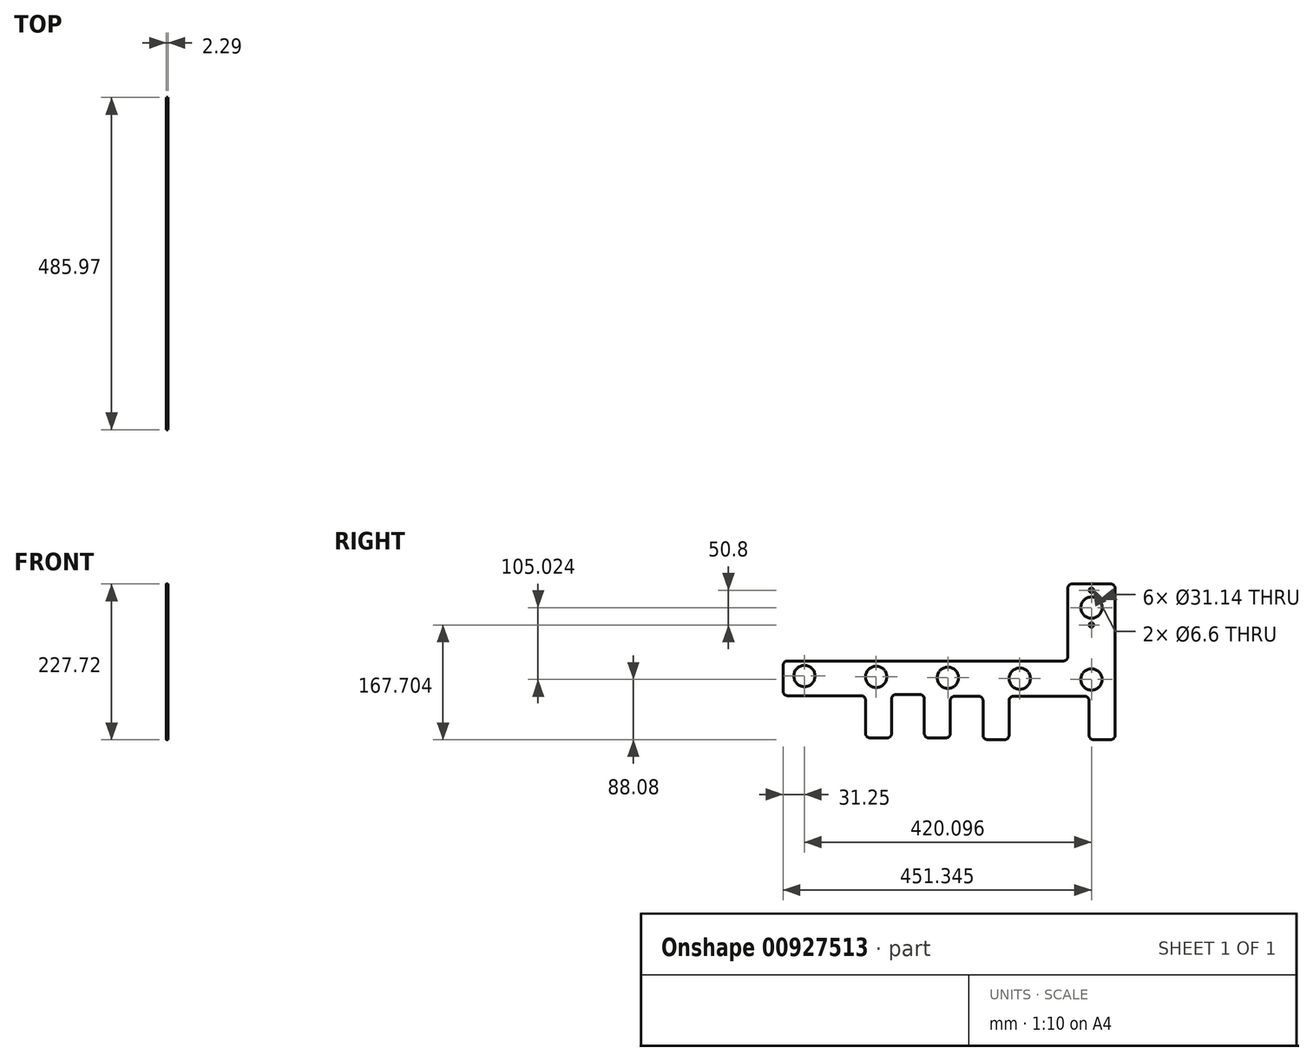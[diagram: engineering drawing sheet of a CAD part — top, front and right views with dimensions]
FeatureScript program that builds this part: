
annotation { "Feature Type Name" : "Feature", "Feature Type Description" : "" }
export const myFeature = defineFeature(function(context is Context, id is Id, definition is map)
    precondition{}
    {
        {
            var Q0;
            Q0=qCreatedBy(makeId("Right.planeOp"),FACE);
            var sketch = newSketch(context, id + "F0", { "sketchPlane" : qUnion([Q0])});
            skLineSegment(sketch, "E0.bottom", {"start": v(-215.45, 21.92) * mm, "end": v(188.58, 21.92) * mm});
            skLineSegment(sketch, "E0.top", {"start": v(-215.45, -28.88) * mm, "end": v(-107.45, -28.88) * mm});
            skLineSegment(sketch, "E0.left", {"start": v(-221.8, 15.57) * mm, "end": v(-221.8, -22.53) * mm});
            skCircle(sketch, "E1", {"center": v(-190.55, 0) * mm, "radius": 15.57 * mm});
            skCircle(sketch, "E2", {"center": v(-85.53, -1.27) * mm, "radius": 15.57 * mm});
            skCircle(sketch, "E3", {"center": v(19.5, -2.54) * mm, "radius": 15.57 * mm});
            skCircle(sketch, "E4", {"center": v(124.52, -3.81) * mm, "radius": 15.57 * mm});
            skCircle(sketch, "E5", {"center": v(229.55, -5.08) * mm, "radius": 15.57 * mm});
            skPoint(sketch, "E6.visualSharp", {"position": v(-221.8, 21.92) * mm});
            skArc(sketch, "E6.filletArc", {"start": v(-215.45, 21.92) * mm, "mid": v(-219.94, 20.06) * mm, "end": v(-221.8, 15.57) * mm});
            skPoint(sketch, "E7.visualSharp", {"position": v(264.17, 21.92) * mm});
            skLineSegment(sketch, "E8.left", {"start": v(-101.1, -35.23) * mm, "end": v(-101.1, -84.27) * mm});
            skLineSegment(sketch, "E8.right", {"start": v(108.95, -36) * mm, "end": v(108.95, -86.8) * mm});
            skArc(sketch, "E9.filletArc", {"start": v(-101.1, -35.23) * mm, "mid": v(-102.96, -30.74) * mm, "end": v(-107.45, -28.88) * mm});
            skLineSegment(sketch, "E10", {"start": v(115.3, -29.66) * mm, "end": v(219.72, -29.66) * mm});
            skPoint(sketch, "E11.visualSharp", {"position": v(108.95, -29.66) * mm});
            skArc(sketch, "E11.filletArc", {"start": v(115.3, -29.66) * mm, "mid": v(110.81, -31.52) * mm, "end": v(108.95, -36) * mm});
            skPoint(sketch, "E12.visualSharp", {"position": v(264.17, -29.66) * mm});
            skPoint(sketch, "E13.visualSharp", {"position": v(-221.8, -28.88) * mm});
            skArc(sketch, "E13.filletArc", {"start": v(-221.8, -22.53) * mm, "mid": v(-219.94, -27.02) * mm, "end": v(-215.45, -28.88) * mm});
            skPoint(sketch, "E14.visualSharp", {"position": v(-101.1, -90.62) * mm});
            skArc(sketch, "E14.filletArc", {"start": v(-101.1, -84.27) * mm, "mid": v(-99.24, -88.76) * mm, "end": v(-94.75, -90.62) * mm});
            skPoint(sketch, "E15.visualSharp", {"position": v(108.95, -93.16) * mm});
            skArc(sketch, "E15.filletArc", {"start": v(102.6, -93.16) * mm, "mid": v(107.1, -91.3) * mm, "end": v(108.95, -86.8) * mm});
            skLineSegment(sketch, "E16", {"start": v(70.85, -86.8) * mm, "end": v(70.85, -36) * mm});
            skLineSegment(sketch, "E17", {"start": v(-63, -84.27) * mm, "end": v(-63, -33.47) * mm});
            skLineSegment(sketch, "E18", {"start": v(22.97, -84.27) * mm, "end": v(22.97, -36) * mm});
            skLineSegment(sketch, "E19", {"start": v(-15.12, -84.27) * mm, "end": v(-15.12, -33.47) * mm});
            skLineSegment(sketch, "E20", {"start": v(102.6, -93.16) * mm, "end": v(77.2, -93.16) * mm});
            skLineSegment(sketch, "E21", {"start": v(16.62, -90.62) * mm, "end": v(-8.77, -90.62) * mm});
            skLineSegment(sketch, "E22", {"start": v(-69.35, -90.62) * mm, "end": v(-94.75, -90.62) * mm});
            skLineSegment(sketch, "E23", {"start": v(64.5, -29.66) * mm, "end": v(29.32, -29.66) * mm});
            skLineSegment(sketch, "E24", {"start": v(-21.47, -27.12) * mm, "end": v(-56.65, -27.12) * mm});
            skPoint(sketch, "E25.visualSharp", {"position": v(70.85, -93.16) * mm});
            skArc(sketch, "E25.filletArc", {"start": v(70.85, -86.8) * mm, "mid": v(72.71, -91.3) * mm, "end": v(77.2, -93.16) * mm});
            skPoint(sketch, "E26.visualSharp", {"position": v(70.85, -29.66) * mm});
            skArc(sketch, "E26.filletArc", {"start": v(70.85, -36) * mm, "mid": v(69, -31.52) * mm, "end": v(64.5, -29.66) * mm});
            skPoint(sketch, "E27.visualSharp", {"position": v(22.97, -29.66) * mm});
            skArc(sketch, "E27.filletArc", {"start": v(29.32, -29.66) * mm, "mid": v(24.83, -31.52) * mm, "end": v(22.97, -36) * mm});
            skPoint(sketch, "E28.visualSharp", {"position": v(22.97, -90.62) * mm});
            skArc(sketch, "E28.filletArc", {"start": v(16.62, -90.62) * mm, "mid": v(21.11, -88.76) * mm, "end": v(22.97, -84.27) * mm});
            skPoint(sketch, "E29.visualSharp", {"position": v(-15.12, -90.62) * mm});
            skArc(sketch, "E29.filletArc", {"start": v(-15.12, -84.27) * mm, "mid": v(-13.26, -88.76) * mm, "end": v(-8.77, -90.62) * mm});
            skPoint(sketch, "E30.visualSharp", {"position": v(-15.12, -27.12) * mm});
            skArc(sketch, "E30.filletArc", {"start": v(-15.12, -33.47) * mm, "mid": v(-16.98, -28.98) * mm, "end": v(-21.47, -27.12) * mm});
            skPoint(sketch, "E31.visualSharp", {"position": v(-63, -27.12) * mm});
            skArc(sketch, "E31.filletArc", {"start": v(-56.65, -27.12) * mm, "mid": v(-61.14, -28.98) * mm, "end": v(-63, -33.47) * mm});
            skPoint(sketch, "E32.visualSharp", {"position": v(-63, -90.62) * mm});
            skArc(sketch, "E32.filletArc", {"start": v(-69.35, -90.62) * mm, "mid": v(-64.86, -88.76) * mm, "end": v(-63, -84.27) * mm});
            skLineSegment(sketch, "E33", {"start": v(264.17, 21.92) * mm, "end": v(264.17, -23.3) * mm});
            skLineSegment(sketch, "E34", {"start": v(257.82, -29.66) * mm, "end": v(254.45, -29.66) * mm});
            skCircle(sketch, "E35", {"center": v(229.55, 99.94) * mm, "radius": 15.57 * mm});
            skLineSegment(sketch, "E36", {"start": v(264.17, 21.92) * mm, "end": v(264.17, 128.21) * mm});
            skLineSegment(sketch, "E37", {"start": v(257.82, 134.56) * mm, "end": v(201.28, 134.56) * mm});
            skLineSegment(sketch, "E38", {"start": v(194.93, 128.21) * mm, "end": v(194.93, 28.27) * mm});
            skCircle(sketch, "E39", {"center": v(229.55, 125.34) * mm, "radius": 3.3 * mm});
            skCircle(sketch, "E40", {"center": v(229.55, 74.54) * mm, "radius": 3.3 * mm});
            skPoint(sketch, "E41.visualSharp", {"position": v(194.93, 134.56) * mm});
            skArc(sketch, "E41.filletArc", {"start": v(201.28, 134.56) * mm, "mid": v(196.78, 132.7) * mm, "end": v(194.93, 128.21) * mm});
            skPoint(sketch, "E42.visualSharp", {"position": v(264.17, 134.56) * mm});
            skArc(sketch, "E42.filletArc", {"start": v(264.17, 128.21) * mm, "mid": v(262.3, 132.7) * mm, "end": v(257.82, 134.56) * mm});
            skPoint(sketch, "E43.newPointA", {"position": v(194.93, 21.92) * mm});
            skArc(sketch, "E43.filletArc", {"start": v(188.58, 21.92) * mm, "mid": v(193.07, 23.78) * mm, "end": v(194.93, 28.27) * mm});
            skArc(sketch, "E44.filletArc", {"start": v(257.82, -29.66) * mm, "mid": v(262.3, -27.8) * mm, "end": v(264.17, -23.3) * mm});
            skLineSegment(sketch, "E45", {"start": v(264.17, -23.3) * mm, "end": v(264.17, -86.8) * mm});
            skLineSegment(sketch, "E46", {"start": v(226.07, -36) * mm, "end": v(226.07, -86.8) * mm});
            skLineSegment(sketch, "E47", {"start": v(232.42, -93.16) * mm, "end": v(257.82, -93.16) * mm});
            skPoint(sketch, "E48.newPointA", {"position": v(226.07, -29.66) * mm});
            skArc(sketch, "E48.filletArc", {"start": v(226.07, -36) * mm, "mid": v(224.2, -31.52) * mm, "end": v(219.72, -29.66) * mm});
            skPoint(sketch, "E49.visualSharp", {"position": v(226.07, -93.16) * mm});
            skArc(sketch, "E49.filletArc", {"start": v(226.07, -86.8) * mm, "mid": v(227.93, -91.3) * mm, "end": v(232.42, -93.16) * mm});
            skPoint(sketch, "E50.visualSharp", {"position": v(264.17, -93.16) * mm});
            skArc(sketch, "E50.filletArc", {"start": v(257.82, -93.16) * mm, "mid": v(262.3, -91.3) * mm, "end": v(264.17, -86.8) * mm});
            skSolve(sketch);
        }
        {
            var Q0;
            Q0=makeQuery(id+"F0.imprint","IMPRINT",FACE,{"disambiguationData":[TD([[makeQuery(id+"F0.imprint","IMPRINT",EDGE,{"derivedFrom":sQuery(id+"F0.wireOp",EDGE,"E0.bottom")}),-1.0]])]});
            extrude(context, id + "F1", {"entities" : qUnion([Q0]), "depth" : 2.3 * mm, "offsetDistance" : 25.4 * mm});
        }
    });
